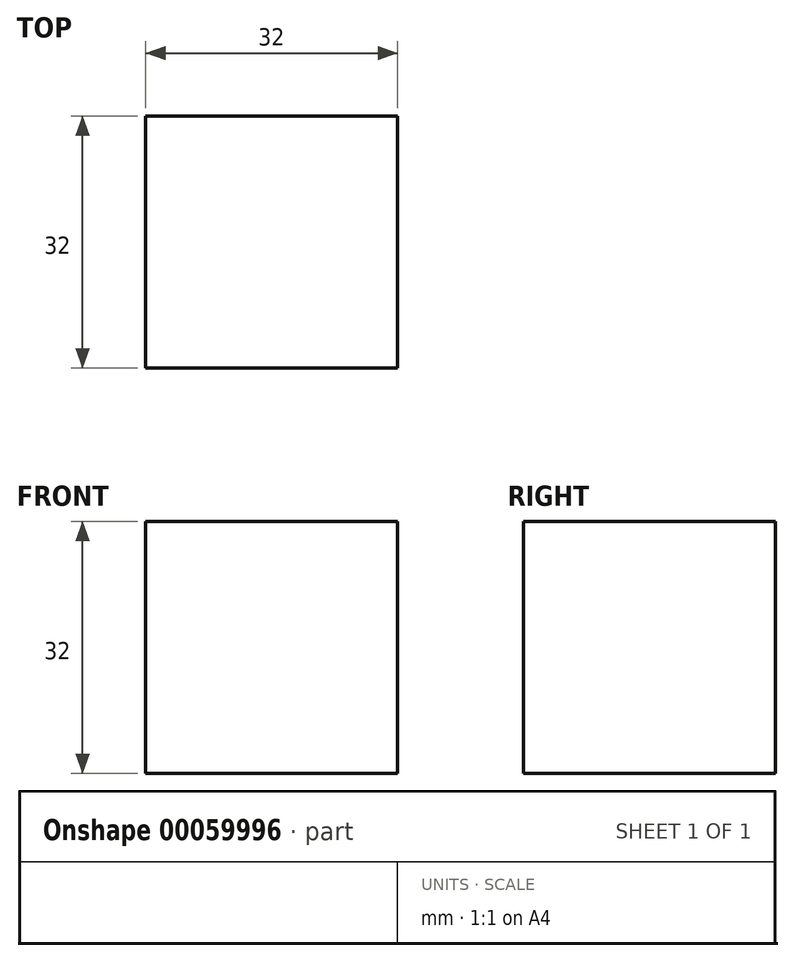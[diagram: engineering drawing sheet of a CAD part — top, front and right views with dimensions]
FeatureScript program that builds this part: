
annotation { "Feature Type Name" : "Feature", "Feature Type Description" : "" }
export const myFeature = defineFeature(function(context is Context, id is Id, definition is map)
    precondition{}
    {
        {
            var Q0;
            Q0=qCreatedBy(makeId("Top.planeOp"),FACE);
            var sketch = newSketch(context, id + "F0", { "sketchPlane" : qUnion([Q0])});
            skLineSegment(sketch, "E0.bottom", {"start": v(0, 0) * mm, "end": v(32, 0) * mm});
            skLineSegment(sketch, "E0.top", {"start": v(0, 32) * mm, "end": v(32, 32) * mm});
            skLineSegment(sketch, "E0.left", {"start": v(0, 0) * mm, "end": v(0, 32) * mm});
            skLineSegment(sketch, "E0.right", {"start": v(32, 0) * mm, "end": v(32, 32) * mm});
            skSolve(sketch);
        }
        {
            var Q0;
            Q0=makeQuery(id+"F0.imprint","IMPRINT",FACE,{"disambiguationData":[TD([[makeQuery(id+"F0.imprint","IMPRINT",EDGE,{"derivedFrom":sQuery(id+"F0.wireOp",EDGE,"E0.bottom")}),1.0]])]});
            extrude(context, id + "F1", {"entities" : qUnion([Q0]), "depth" : 32 * mm});
        }
    });
